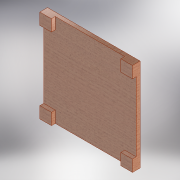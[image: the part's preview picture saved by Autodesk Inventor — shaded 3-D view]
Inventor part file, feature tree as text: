
AUTODESK INVENTOR PART (.ipt)
format: ipt  version: 2018.2 (Build 222227000, 227)  size: 145,408 bytes
history: native  units: mm
features: extrude x2, sketch x2
ambient origin geometry x8: Origin, YZ Plane, XZ Plane, XY Plane, X Axis, Y Axis, Z Axis, Center Point
bodies: Solid1 (feature_tree)
feature tree (4):
  extrude  "Extrusion1"  Depth=304.8mm
  extrude  "Extrusion2"  Depth=38.1mm
  sketch  "Sketch1"  dims[d0=304.8mm d1=304.8mm]
  sketch  "Sketch2"  dims[d2=12.7mm d3=0.0mm d7=38.1mm d8=38.1mm d9=12.7mm d10=0.0mm]
